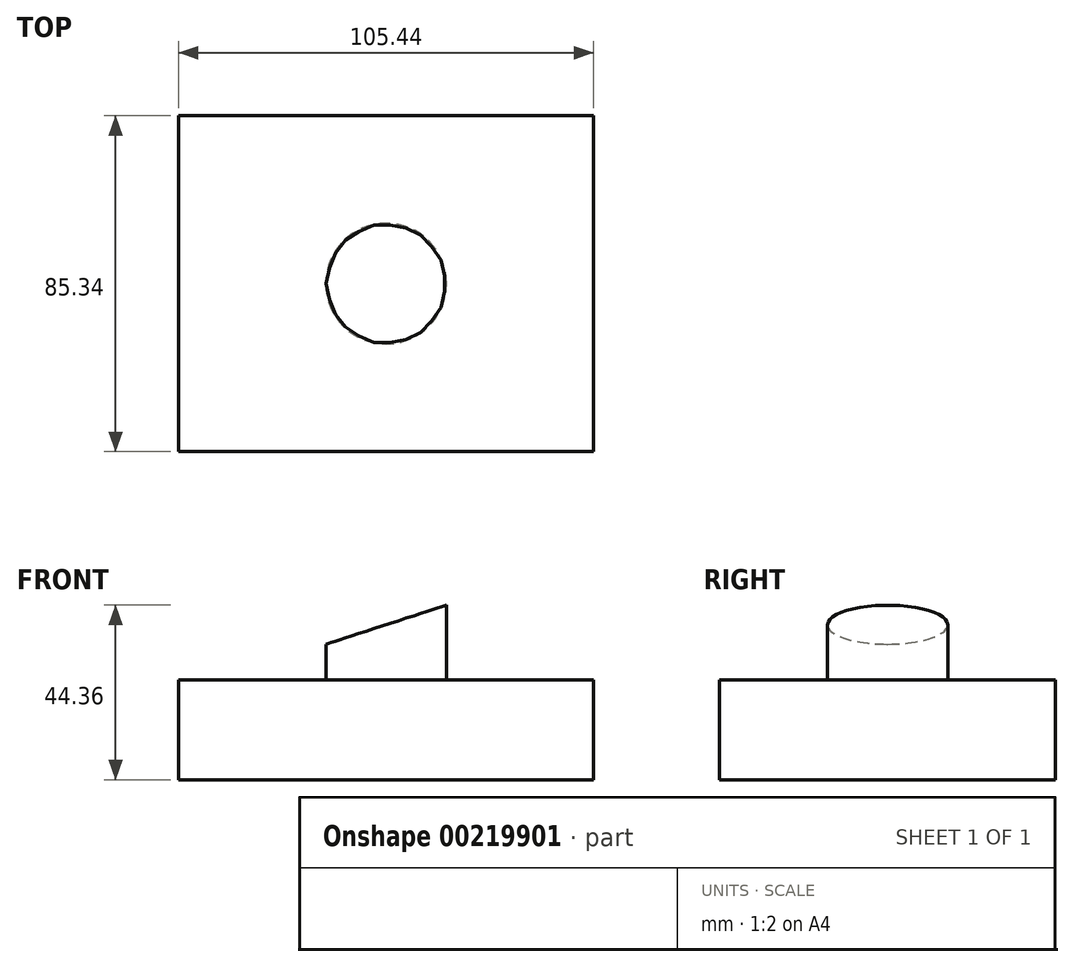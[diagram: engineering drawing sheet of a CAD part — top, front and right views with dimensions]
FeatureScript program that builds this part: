
annotation { "Feature Type Name" : "Feature", "Feature Type Description" : "" }
export const myFeature = defineFeature(function(context is Context, id is Id, definition is map)
    precondition{}
    {
        {
            var Q0;
            Q0=qCreatedBy(makeId("Top.planeOp"),FACE);
            var sketch = newSketch(context, id + "F0", { "sketchPlane" : qUnion([Q0])});
            skLineSegment(sketch, "E0.bottom", {"start": v(52.72, -42.67) * mm, "end": v(-52.72, -42.67) * mm});
            skLineSegment(sketch, "E0.top", {"start": v(52.72, 42.67) * mm, "end": v(-52.72, 42.67) * mm});
            skLineSegment(sketch, "E0.left", {"start": v(52.72, -42.67) * mm, "end": v(52.72, 42.67) * mm});
            skLineSegment(sketch, "E0.right", {"start": v(-52.72, -42.67) * mm, "end": v(-52.72, 42.67) * mm});
            skPoint(sketch, "E0.middle", {"position": v(0, 0) * mm});
            skSolve(sketch);
        }
        {
            var Q0;
            Q0 = qSketchRegion(id + "F0", true);
            extrude(context, id + "F1", {"entities" : qUnion([Q0]), "depth" : 25.4 * mm});
        }
        {
            var Q0;
            Q0=makeQuery(id+"F1.opExtrude","CAP_FACE",FACE,{"disambiguationData":[OSD([sQuery(id+"F0.wireOp",EDGE,"E0.bottom"),sQuery(id+"F0.wireOp",EDGE,"E0.top"),sQuery(id+"F0.wireOp",EDGE,"E0.left"),sQuery(id+"F0.wireOp",EDGE,"E0.right")])],"isStart":false});
            var sketch = newSketch(context, id + "F2", { "sketchPlane" : qUnion([Q0])});
            skCircle(sketch, "E1", {"center": v(0, 0) * mm, "radius": 15.31 * mm});
            skSolve(sketch);
        }
        {
            var Q0;
            Q0 = qSketchRegion(id + "F2", true);
            extrude(context, id + "F3", {"entities" : qUnion([Q0]), "operationType" : NewBodyOperationType.ADD, "depth" : 25.4 * mm});
        }
        {
            var Q0;
            Q0=makeQuery(id+"F1.opExtrude","SWEPT_FACE",FACE,{"disambiguationData":[OSD([sQuery(id+"F0.wireOp",EDGE,"E0.top")])]});
            var sketch = newSketch(context, id + "F4", { "sketchPlane" : qUnion([Q0])});
            skLineSegment(sketch, "E2", {"start": v(-29.1, 48.84) * mm, "end": v(23.55, 31.75) * mm});
            skLineSegment(sketch, "E3", {"start": v(23.55, 31.75) * mm, "end": v(32.44, 59.12) * mm});
            skLineSegment(sketch, "E4", {"start": v(32.44, 59.12) * mm, "end": v(-27.48, 63.62) * mm});
            skLineSegment(sketch, "E5", {"start": v(-27.48, 63.62) * mm, "end": v(-29.1, 48.84) * mm});
            skSolve(sketch);
        }
        {
            var Q0;
            Q0 = qSketchRegion(id + "F4", true);
            extrude(context, id + "F5", {"entities" : qUnion([Q0]), "operationType" : NewBodyOperationType.REMOVE, "oppositeDirection" : true, "depth" : 87.38 * mm});
        }
    });
